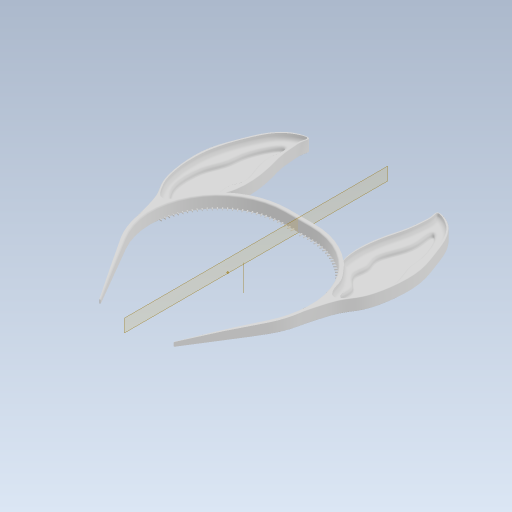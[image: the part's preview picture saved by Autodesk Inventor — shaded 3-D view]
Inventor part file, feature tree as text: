
AUTODESK INVENTOR PART (.ipt)
format: ipt  version: 2023 (Build 270158030, 158C)  size: 2,666,496 bytes
history: native  units: in
note: dims shown in document units (in); Inventor stores cm internally (conversion verified against a paired STEP export)
features: fillet x19, extrude x12, sketch x11, projected_geometry x6, chamfer x2, other x1, pattern_circular x1, mirror x1
ambient origin geometry x8: Origin, YZ Plane, XZ Plane, XY Plane, X Axis, Y Axis, Z Axis, Center Point
bodies: Solid1 (feature_tree), Solid2 (feature_tree)
feature tree (53):
  extrude  "Extrusion1"  Depth=0.1181in
  extrude  "Extrusion2"  Depth=0.3937in TaperAngle=0.0deg
  fillet  "Fillet2"  Radius=0.0433in
  other  "Work Axis1"
  pattern_circular  "Circular Pattern1"  Count=30  [1 undecoded]
  extrude  "Extrusion4"  Depth=4.3307in
  fillet  "Fillet6"  Radius=25.1969in
  fillet  "Fillet7"  Radius=0.7087in
  fillet  "Fillet8"  Radius=4.3307in
  extrude  "Extrusion10"  TaperAngle=0.0deg  [1 undecoded]
  extrude  "Extrusion11"  Depth=0.0394in
  extrude  "Extrusion12"  Depth=0.3937in TaperAngle=0.0deg
  fillet  "Fillet32"  Radius=0.315in
  fillet  "Fillet33"  Radius=0.0591in
  fillet  "Fillet35"  Radius=0.0591in
  chamfer  "Chamfer2"  Distance=0.3346in
  fillet  "Fillet36"  Radius=2.3495in
  extrude  "Extrusion13"  Depth=2.0826in
  mirror  "Mirror1"
  fillet  "Fillet30"  Radius=1.4138in
  fillet  "Fillet28"  Radius=2.5284in
  fillet  "Fillet19"  Radius=1.4901in
  extrude  "Extrusion5"  Depth=2.5146in
  extrude  "Extrusion7"  Depth=2.7368in
  extrude  "Extrusion6"  Depth=1.4623in
  fillet  "Fillet20"  Radius=0.488in
  fillet  "Fillet21"  Radius=0.3104in
  fillet  "Fillet22"  Radius=0.2859in
  fillet  "Fillet23"  Radius=0.2088in
  fillet  "Fillet24"  Radius=0.2171in
  fillet  "Fillet25"  Radius=0.23in
  fillet  "Fillet26"  Radius=0.2362in
  extrude  "Extrusion8"  Depth=0.0787in
  fillet  "Fillet27"  Radius=0.0787in
  extrude  "Extrusion9"  Depth=0.0394in
  chamfer  "Chamfer1"  Distance=0.0394in
  sketch  "Sketch1"  dims[d23=2.2638in d25=0.1181in]
  sketch  "Sketch2"  dims[d27=0.1181in d30=0.3937in d31=0.0in d48=0.0433in d49=0.0in]
  sketch  "Sketch7"  dims[d50=0.0118in]
  sketch  "Sketch8"  dims[d57=0.0787in d58=0.0157in d61=11.811in d62=-0.6184in]
  sketch  "Sketch9"  dims[d65=3.1496in d76=4.3307in d77=25.1969in d78=0.7087in d79=4.3307in]
  sketch  "Sketch11"  dims[d80=0.3937in d81=0.0in d82=0.0in]
  sketch  "Sketch12"  dims[d86=0.0394in d87=0.0394in]
  projected_geometry  "Projected Loop1"
  sketch  "Sketch13"  dims[d88=0.0236in d104=0.3937in d105=0.0in d107=0.315in d108=0.0in d121=0.0591in d122=0.0591in]
  projected_geometry  "Projected Loop2"
  projected_geometry  "Projected Loop3"
  sketch  "Sketch14"  dims[d123=1.378in d125=0.3346in d126=0.0in d130=2.3495in]
  projected_geometry  "Projected Loop4"
  sketch  "Sketch16"  dims[d131=2.2052in d132=2.0826in d133=1.4138in d134=2.5284in d135=1.4901in]
  projected_geometry  "Projected Loop5"
  sketch  "Sketch18"  dims[d136=2.1896in d137=2.5146in d138=2.7368in d139=1.4623in d140=0.488in d141=0.3104in d142=0.2859in d143=0.2088in d144=0.2171in d145=0.23in d147=0.2362in d148=0.0787in d149=0.0787in d150=0.0394in d153=0.0394in d154=0.1181in d155=0.0787in d156=0.0787in d158=23.622in d159=1.9685in d161=7.8078in d162=2.3622in d163=0.7874in d164=0.9817in d165=0.0in d167=0.0787in d168=0.1969in d169=0.1969in d170=0.1181in d171=0.0197in d172=0.0079in d173=0.0394in d174=0.0197in d175=0.0197in d182=0.0984in d183=0.0394in d184=0.0984in d185=0.0394in d186=0.0591in d187=0.0394in d188=0.0197in d189=0.076in d190=0.0in d191=0.0in d192=0.0079in d193=0.0197in d194=0.0787in d195=45.0deg d196=0.0in d197=0.0in d199=0.3937in d200=0.0in d201=0.3543in d202=0.0in d203=0.315in d205=0.1969in d206=0.0in d207=0.1181in d209=0.0118in d210=0.1181in d212=0.0394in d213=0.015in d214=0.0787in d215=45.0deg d216=0.7874in d217=0.4331in d218=2.3622in d219=0.4331in d220=0.0984in d221=0.3937in d222=0.1181in d223=0.0787in d224=0.1969in d225=0.0in]
  projected_geometry  "Projected Loop6"
note: 2 required parameter values undecoded (feature->parameter linkage not recoverable at this tier; creation-order binding heuristic only, values carry confidence <= 0.55)
